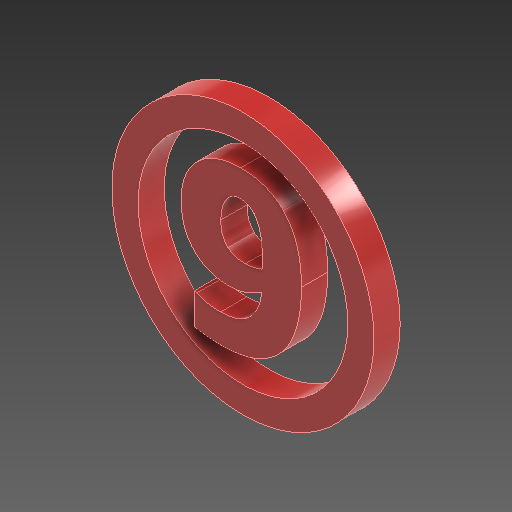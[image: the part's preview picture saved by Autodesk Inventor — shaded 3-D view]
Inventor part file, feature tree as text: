
AUTODESK INVENTOR PART (.ipt)
format: ipt  version: 2020 (Build 240168000, 168)  size: 214,528 bytes
history: native  units: mm
features: other x5, extrude x2, sketch x2
ambient origin geometry x8: Origin, YZ Plane, XZ Plane, XY Plane, X Axis, Y Axis, Z Axis, Center Point
bodies: Body1 (feature_tree)
feature tree (9):
  other  "自動販賣機.ipt"
  extrude  "擠出1"  Depth=10.0mm
  extrude  "擠出2"  Depth=10.0mm TaperAngle=0.0deg
  other  "實體49::自動販賣機.ipt"
  other  "標籤特徵1"
  sketch  "草圖1"
  sketch  "草圖2"
  other  "實體1"
  other  "投影切割邊1"
